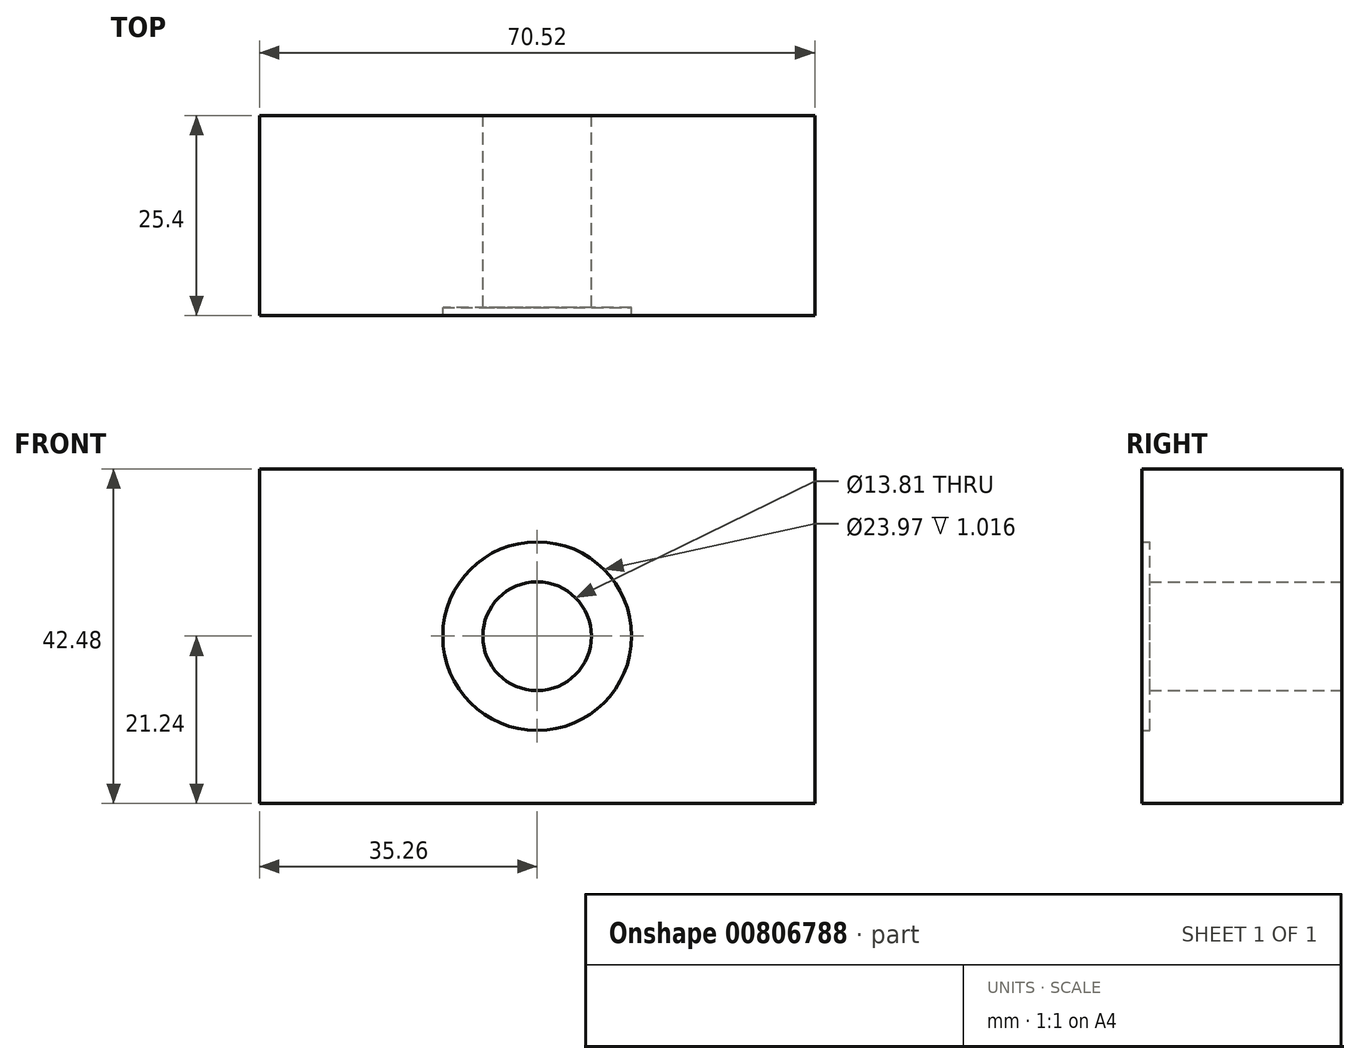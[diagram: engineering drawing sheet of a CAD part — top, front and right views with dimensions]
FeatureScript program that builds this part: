
annotation { "Feature Type Name" : "Feature", "Feature Type Description" : "" }
export const myFeature = defineFeature(function(context is Context, id is Id, definition is map)
    precondition{}
    {
        {
            var Q0;
            Q0=qCreatedBy(makeId("Front.planeOp"),FACE);
            var sketch = newSketch(context, id + "F0", { "sketchPlane" : qUnion([Q0])});
            skLineSegment(sketch, "E0.bottom", {"start": v(-35.26, 21.24) * mm, "end": v(35.26, 21.24) * mm});
            skLineSegment(sketch, "E0.top", {"start": v(-35.26, -21.24) * mm, "end": v(35.26, -21.24) * mm});
            skLineSegment(sketch, "E0.left", {"start": v(-35.26, 21.24) * mm, "end": v(-35.26, -21.24) * mm});
            skLineSegment(sketch, "E0.right", {"start": v(35.26, 21.24) * mm, "end": v(35.26, -21.24) * mm});
            skPoint(sketch, "E0.middle", {"position": v(0, 0) * mm});
            skCircle(sketch, "E1", {"center": v(0, 0) * mm, "radius": 11.99 * mm});
            skCircle(sketch, "E2", {"center": v(0, 0) * mm, "radius": 6.9 * mm});
            skSolve(sketch);
        }
        {
            var Q0;
            Q0=makeQuery(id+"F0.imprint","IMPRINT",FACE,{"disambiguationData":[TD([[makeQuery(id+"F0.imprint","IMPRINT",EDGE,{"derivedFrom":sQuery(id+"F0.wireOp",EDGE,"E1")}),1.0]])]});
            extrude(context, id + "F1", {"entities" : qUnion([Q0]), "depth" : 24.38 * mm, "offsetDistance" : 25.4 * mm});
        }
        {
            var Q0;
            Q0=makeQuery(id+"F0.imprint","IMPRINT",FACE,{"disambiguationData":[TD([[makeQuery(id+"F0.imprint","IMPRINT",EDGE,{"derivedFrom":sQuery(id+"F0.wireOp",EDGE,"E0.bottom")}),-1.0]])]});
            extrude(context, id + "F2", {"entities" : qUnion([Q0]), "operationType" : NewBodyOperationType.ADD, "depth" : 25.4 * mm, "offsetDistance" : 25.4 * mm});
        }
        {
            var Q0;
            Q0=sQuery(id+"F0.wireOp",EDGE,"E2");
            var Q1;
            Q1=sQuery(id+"F0.wireOp",EDGE,"E1");
            extrude(context, id + "F3", {"bodyType" : ToolBodyType.SURFACE, "surfaceEntities" : qUnion([Q0, Q1]), "depth" : 50.8 * mm, "offsetDistance" : 25.4 * mm});
        }
    });
